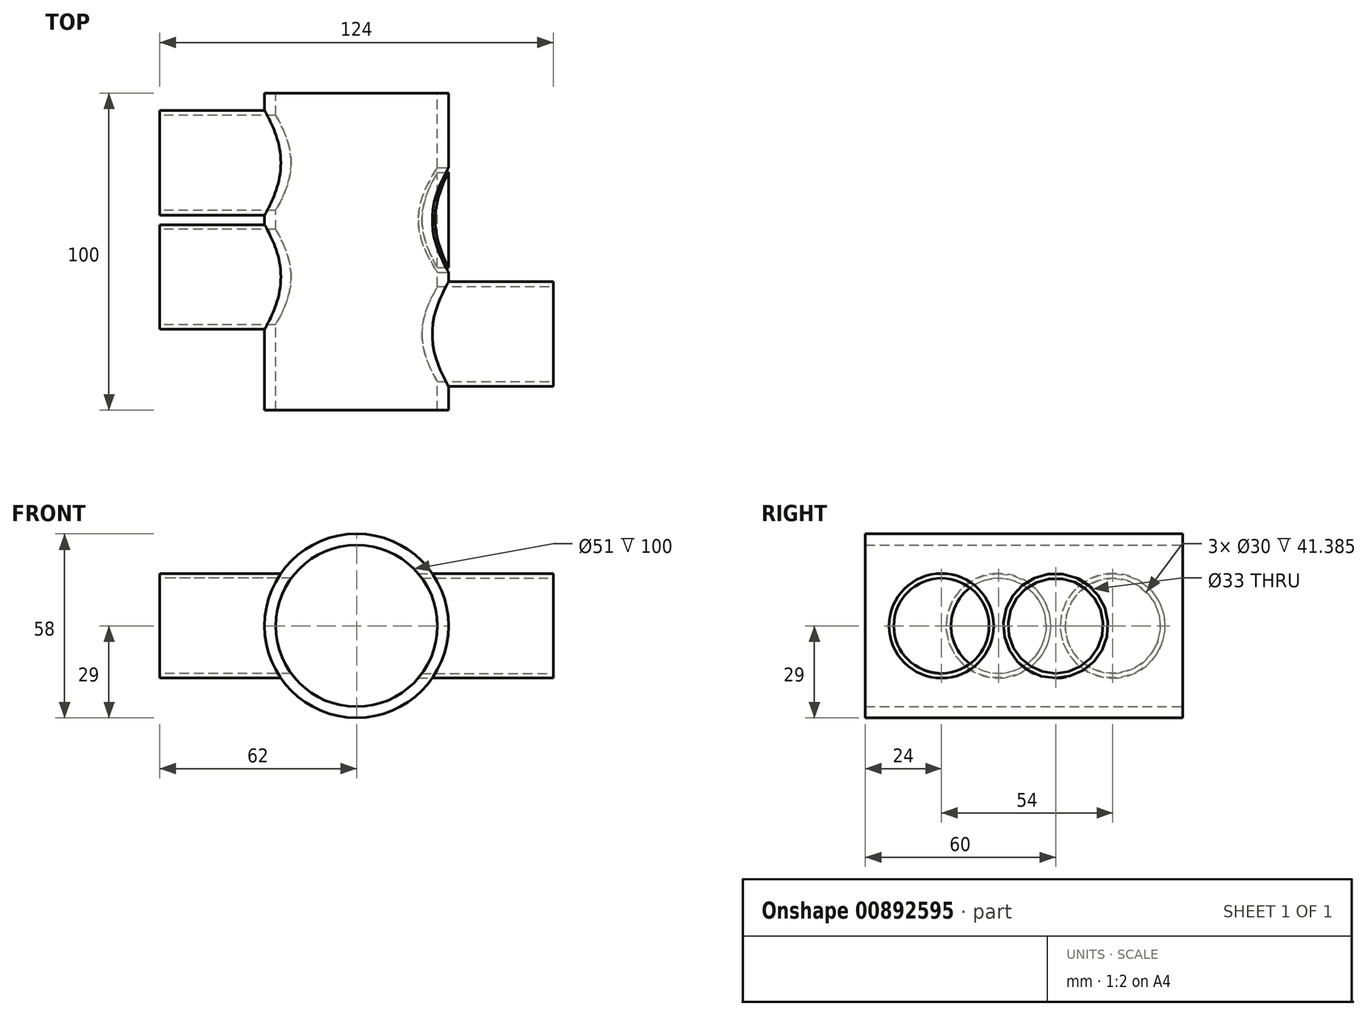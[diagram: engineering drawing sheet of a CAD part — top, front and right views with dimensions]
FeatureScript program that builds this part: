
annotation { "Feature Type Name" : "Feature", "Feature Type Description" : "" }
export const myFeature = defineFeature(function(context is Context, id is Id, definition is map)
    precondition{}
    {
        {
            var Q0;
            Q0=qCreatedBy(makeId("Front.planeOp"),FACE);
            var sketch = newSketch(context, id + "F0", { "sketchPlane" : qUnion([Q0])});
            skCircle(sketch, "E0", {"center": v(0, 0) * mm, "radius": 25.5 * mm});
            skLineSegment(sketch, "E1", {"start": v(0, 0) * mm, "end": v(62, 0) * mm, "construction": true});
            skLineSegment(sketch, "E2", {"start": v(62, 0) * mm, "end": v(62, 12) * mm});
            skLineSegment(sketch, "E3", {"start": v(62, 12) * mm, "end": v(22.5, 12) * mm});
            skCircle(sketch, "E4", {"center": v(0, 0) * mm, "radius": 29 * mm});
            skLineSegment(sketch, "E5", {"start": v(0, 0) * mm, "end": v(0, 29) * mm, "construction": true});
            skLineSegment(sketch, "E6.MirrorCS", {"start": v(0, 0) * mm, "end": v(-62, 0) * mm, "construction": true});
            skLineSegment(sketch, "E7.MirrorCS", {"start": v(-62, 12) * mm, "end": v(-22.5, 12) * mm});
            skLineSegment(sketch, "E8.MirrorCS", {"start": v(-62, 0) * mm, "end": v(-62, 12) * mm});
            skSolve(sketch);
        }
        {
            var Q0;
            Q0=makeQuery(id+"F0.imprint","IMPRINT",FACE,{"disambiguationData":[TD([[makeQuery(id+"F0.imprint","IMPRINT",EDGE,{"derivedFrom":sQuery(id+"F0.wireOp",EDGE,"E0")}),-1.0]])]});
            extrude(context, id + "F1", {"entities" : qUnion([Q0]), "depth" : 100 * mm, "offsetDistance" : 25 * mm, "symmetric" : true});
        }
        {
            var Q0;
            Q0=qCreatedBy(makeId("Right.planeOp"),FACE);
            var Q1;
            Q1=sQuery(id+"F0.wireOp",VERTEX,"E2.end");
            cPlane(context, id + "F2", {"entities" : qUnion([Q0, Q1]), "cplaneType" : CPlaneType.PLANE_POINT, "offset" : 25 * mm, "width" : 150 * mm, "height" : 150 * mm});
        }
        {
            var Q0;
            Q0=qCreatedBy(id+"F2.planeOp",FACE);
            var sketch = newSketch(context, id + "F3", { "sketchPlane" : qUnion([Q0])});
            skCircle(sketch, "E9", {"center": v(-26, 0) * mm, "radius": 16.5 * mm});
            skCircle(sketch, "E10", {"center": v(-26, 0) * mm, "radius": 15 * mm});
            skLineSegment(sketch, "E11", {"start": v(-26, 0) * mm, "end": v(-8, 0) * mm, "construction": true});
            skLineSegment(sketch, "E12", {"start": v(-8, 0) * mm, "end": v(-8, 29.3) * mm, "construction": true});
            skCircle(sketch, "E13.MirrorC", {"center": v(10, 0) * mm, "radius": 16.5 * mm});
            skCircle(sketch, "E14.MirrorC", {"center": v(10, 0) * mm, "radius": 15 * mm});
            skLineSegment(sketch, "E15", {"start": v(-8, 0) * mm, "end": v(0, 0) * mm, "construction": true});
            skSolve(sketch);
        }
        {
            var Q0;
            Q0=makeQuery(id+"F3.imprint","IMPRINT",FACE,{"disambiguationData":[TD([[makeQuery(id+"F3.imprint","IMPRINT",EDGE,{"derivedFrom":sQuery(id+"F3.wireOp",EDGE,"E9")}),-1.0]])]});
            var Q1;
            Q1=makeQuery(id+"F3.imprint","IMPRINT",FACE,{"disambiguationData":[TD([[makeQuery(id+"F3.imprint","IMPRINT",EDGE,{"derivedFrom":sQuery(id+"F3.wireOp",EDGE,"E9")}),1.0]])]});
            var Q2;
            Q2=makeQuery(id+"F3.imprint","IMPRINT",FACE,{"disambiguationData":[TD([[makeQuery(id+"F3.imprint","IMPRINT",EDGE,{"derivedFrom":sQuery(id+"F3.wireOp",EDGE,"E13.MirrorC")}),-1.0]])]});
            var Q3;
            Q3=makeQuery(id+"F1.opExtrude","SWEPT_FACE",FACE,{"disambiguationData":[OSD([sQuery(id+"F0.wireOp",EDGE,"E4")])]});
            extrude(context, id + "F4", {"entities" : qUnion([Q0, Q1, Q2]), "operationType" : NewBodyOperationType.ADD, "endBound" : BoundingType.UP_TO_SURFACE, "oppositeDirection" : true, "depth" : 25 * mm, "endBoundEntityFace" : qUnion([Q3]), "offsetDistance" : 25 * mm});
        }
        {
            var Q0;
            Q0=makeQuery(id+"F3.imprint","IMPRINT",FACE,{"disambiguationData":[TD([[makeQuery(id+"F3.imprint","IMPRINT",EDGE,{"derivedFrom":sQuery(id+"F3.wireOp",EDGE,"E10")}),1.0]])]});
            var Q1;
            Q1=makeQuery(id+"F3.imprint","IMPRINT",FACE,{"disambiguationData":[TD([[makeQuery(id+"F3.imprint","IMPRINT",EDGE,{"derivedFrom":sQuery(id+"F3.wireOp",EDGE,"E14.MirrorC")}),-1.0]])]});
            extrude(context, id + "F5", {"entities" : qUnion([Q0, Q1]), "operationType" : NewBodyOperationType.REMOVE, "oppositeDirection" : true, "depth" : 50 * mm, "offsetDistance" : 25 * mm});
        }
        {
            var Q0;
            Q0=qCreatedBy(makeId("Right.planeOp"),FACE);
            var Q1;
            Q1=sQuery(id+"F0.wireOp",VERTEX,"E7.MirrorCS.start");
            cPlane(context, id + "F6", {"entities" : qUnion([Q0, Q1]), "cplaneType" : CPlaneType.PLANE_POINT, "offset" : 25 * mm, "width" : 150 * mm, "height" : 150 * mm});
        }
        {
            var Q0;
            Q0=qCreatedBy(id+"F6.planeOp",FACE);
            var sketch = newSketch(context, id + "F7", { "sketchPlane" : qUnion([Q0])});
            skCircle(sketch, "E16", {"center": v(-8, 0) * mm, "radius": 15 * mm});
            skCircle(sketch, "E17", {"center": v(-8, 0) * mm, "radius": 16.5 * mm});
            skLineSegment(sketch, "E18", {"start": v(-8, 0) * mm, "end": v(28, 0) * mm, "construction": true});
            skCircle(sketch, "E19", {"center": v(28, 0) * mm, "radius": 15 * mm});
            skCircle(sketch, "E20", {"center": v(28, 0) * mm, "radius": 16.5 * mm});
            skSolve(sketch);
        }
        {
            var Q0;
            Q0=makeQuery(id+"F7.imprint","IMPRINT",FACE,{"disambiguationData":[TD([[makeQuery(id+"F7.imprint","IMPRINT",EDGE,{"derivedFrom":sQuery(id+"F7.wireOp",EDGE,"E19")}),-1.0]])]});
            var Q1;
            Q1=makeQuery(id+"F7.imprint","IMPRINT",FACE,{"disambiguationData":[TD([[makeQuery(id+"F7.imprint","IMPRINT",EDGE,{"derivedFrom":sQuery(id+"F7.wireOp",EDGE,"E16")}),-1.0]])]});
            var Q2;
            {var subQ0=sQuery(id+"F0.wireOp",EDGE,"E4");Q2=makeQuery(id+"F4.boolean.opBoolean","SPLIT",FACE,{"disambiguationData":[TD([makeQuery(id+"F4.opExtrude","SWEPT_FACE",FACE,{"disambiguationData":[OSD([sQuery(id+"F3.wireOp",EDGE,"E9")])]})])],"derivedFrom":makeQuery(id+"F1.opExtrude","SWEPT_FACE",FACE,{"disambiguationData":[OSD([subQ0])]})});}
            extrude(context, id + "F8", {"entities" : qUnion([Q0, Q1]), "operationType" : NewBodyOperationType.ADD, "endBound" : BoundingType.UP_TO_SURFACE, "depth" : 25 * mm, "endBoundEntityFace" : qUnion([Q2]), "offsetDistance" : 25 * mm});
        }
        {
            var Q0;
            Q0=makeQuery(id+"F7.imprint","IMPRINT",FACE,{"disambiguationData":[TD([[makeQuery(id+"F7.imprint","IMPRINT",EDGE,{"derivedFrom":sQuery(id+"F7.wireOp",EDGE,"E19")}),1.0]])]});
            var Q1;
            Q1=makeQuery(id+"F7.imprint","IMPRINT",FACE,{"disambiguationData":[TD([[makeQuery(id+"F7.imprint","IMPRINT",EDGE,{"derivedFrom":sQuery(id+"F7.wireOp",EDGE,"E16")}),1.0]])]});
            extrude(context, id + "F9", {"entities" : qUnion([Q0, Q1]), "operationType" : NewBodyOperationType.REMOVE, "depth" : 50 * mm, "offsetDistance" : 25 * mm});
        }
    });
